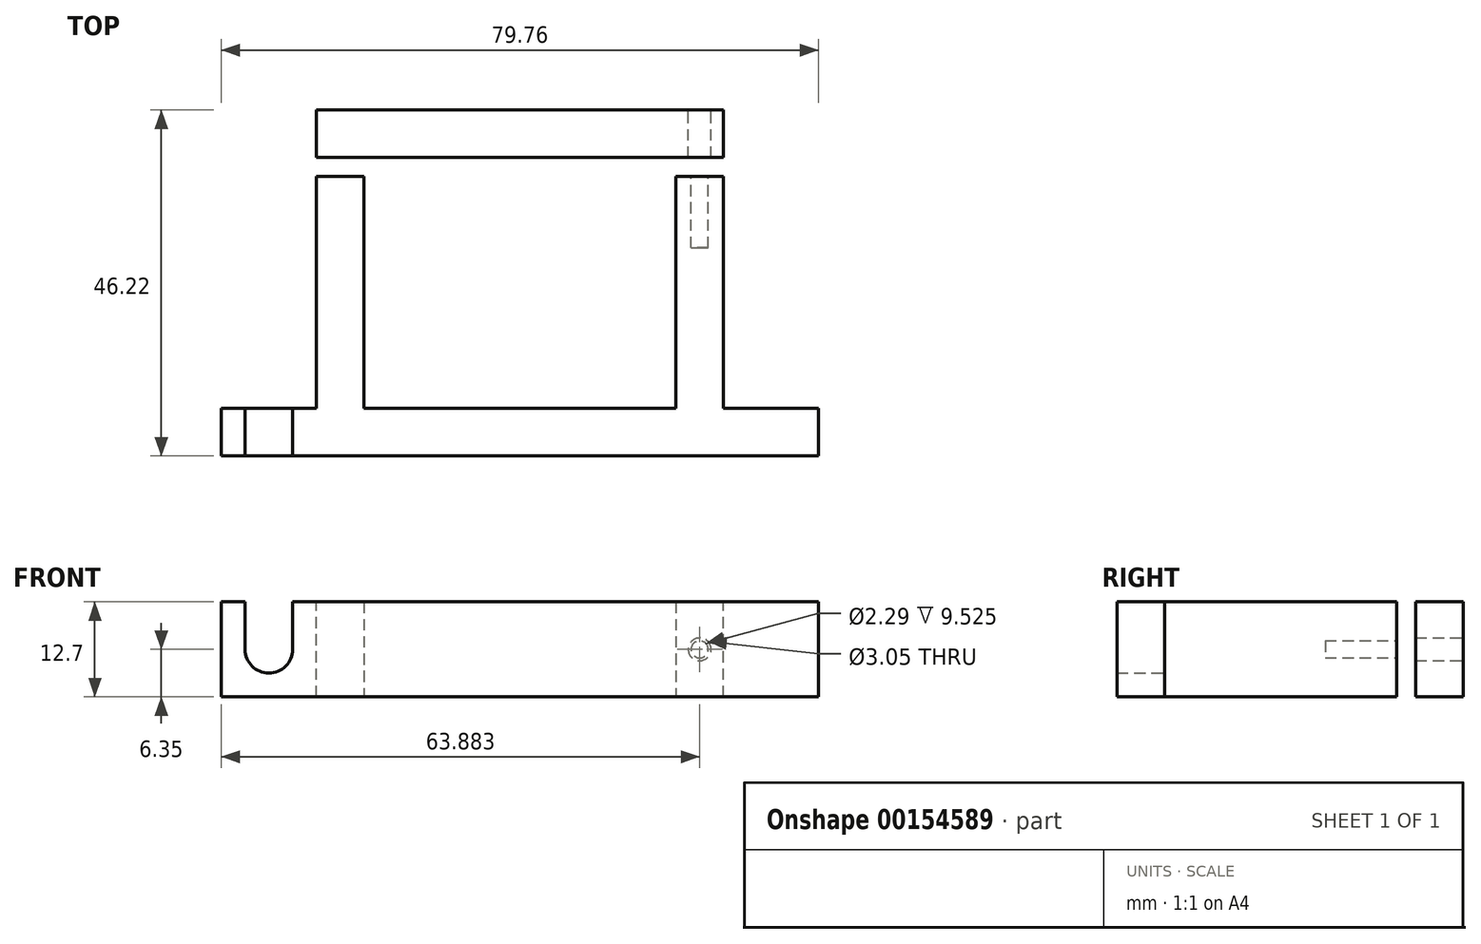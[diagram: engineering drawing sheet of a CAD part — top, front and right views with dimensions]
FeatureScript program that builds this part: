
annotation { "Feature Type Name" : "Feature", "Feature Type Description" : "" }
export const myFeature = defineFeature(function(context is Context, id is Id, definition is map)
    precondition{}
    {
        {
            var Q0;
            Q0=qCreatedBy(makeId("Top.planeOp"),FACE);
            var sketch = newSketch(context, id + "F0", { "sketchPlane" : qUnion([Q0])});
            skLineSegment(sketch, "E0.bottom", {"start": v(-20.83, 16.76) * mm, "end": v(20.83, 16.76) * mm});
            skLineSegment(sketch, "E0.top", {"start": v(-20.83, -16.76) * mm, "end": v(20.83, -16.76) * mm});
            skLineSegment(sketch, "E0.left", {"start": v(-20.83, 16.76) * mm, "end": v(-20.83, -16.76) * mm});
            skLineSegment(sketch, "E0.right", {"start": v(20.83, 16.76) * mm, "end": v(20.83, -16.76) * mm});
            skPoint(sketch, "E0.middle", {"position": v(0, 0) * mm});
            skLineSegment(sketch, "E1.0", {"start": v(27.18, 23.11) * mm, "end": v(27.18, -23.11) * mm});
            skLineSegment(sketch, "E1.1", {"start": v(-27.18, 23.11) * mm, "end": v(27.18, 23.11) * mm});
            skLineSegment(sketch, "E1.2", {"start": v(-27.18, 23.11) * mm, "end": v(-27.18, -23.11) * mm});
            skLineSegment(sketch, "E1.3", {"start": v(-27.18, -23.11) * mm, "end": v(27.18, -23.11) * mm});
            skLineSegment(sketch, "E2", {"start": v(-27.18, -16.76) * mm, "end": v(-39.88, -16.76) * mm});
            skLineSegment(sketch, "E3", {"start": v(-39.88, -16.76) * mm, "end": v(-39.88, -23.11) * mm});
            skLineSegment(sketch, "E4", {"start": v(-39.88, -23.11) * mm, "end": v(-27.18, -23.11) * mm});
            skLineSegment(sketch, "E5", {"start": v(27.18, -16.76) * mm, "end": v(39.88, -16.76) * mm});
            skLineSegment(sketch, "E6", {"start": v(39.88, -16.76) * mm, "end": v(39.88, -23.11) * mm});
            skLineSegment(sketch, "E7", {"start": v(39.88, -23.11) * mm, "end": v(27.18, -23.11) * mm});
            skSolve(sketch);
        }
        {
            var Q0;
            Q0 = qSketchRegion(id + "F0", true);
            extrude(context, id + "F1", {"entities" : qUnion([Q0]), "depth" : 12.7 * mm});
        }
        {
            var Q0;
            Q0=makeQuery(id+"F1.opExtrude","SWEPT_FACE",FACE,{"disambiguationData":[OSD([sQuery(id+"F0.wireOp",EDGE,"E2")])]});
            var sketch = newSketch(context, id + "F2", { "sketchPlane" : qUnion([Q0])});
            skLineSegment(sketch, "E8", {"start": v(39.88, 12.7) * mm, "end": v(27.18, 0) * mm, "construction": true});
            skArc(sketch, "E9", {"start": v(30.35, 6.35) * mm, "mid": v(33.53, 3.17) * mm, "end": v(36.7, 6.35) * mm});
            skPoint(sketch, "E9.startSnap0", {"position": v(33.53, 6.35) * mm});
            skLineSegment(sketch, "E10", {"start": v(36.7, 6.35) * mm, "end": v(36.7, 12.7) * mm});
            skLineSegment(sketch, "E11", {"start": v(36.7, 12.7) * mm, "end": v(30.35, 12.7) * mm});
            skLineSegment(sketch, "E12", {"start": v(30.35, 12.7) * mm, "end": v(30.35, 6.35) * mm});
            skSolve(sketch);
        }
        {
            var Q0;
            Q0 = qSketchRegion(id + "F2", true);
            extrude(context, id + "F3", {"entities" : qUnion([Q0]), "operationType" : NewBodyOperationType.REMOVE, "endBound" : BoundingType.THROUGH_ALL, "oppositeDirection" : true, "depth" : 25.4 * mm});
        }
        {
            var Q0;
            {var subQ0=sQuery(id+"F0.wireOp",EDGE,"E7");var subQ1=sQuery(id+"F0.wireOp",EDGE,"E4");var subQ2=sQuery(id+"F0.wireOp",EDGE,"E1.3");var subQ4=sQuery(id+"F0.wireOp",EDGE,"E1.2");var subQ6=sQuery(id+"F0.wireOp",EDGE,"E1.1");var subQ8=sQuery(id+"F0.wireOp",EDGE,"E1.0");var subQ10=sQuery(id+"F0.wireOp",EDGE,"E0.bottom");var subQ11=makeQuery(id+"F1.opExtrude","SWEPT_FACE",FACE,{"disambiguationData":[OSD([subQ10])]});var subQ12=sQuery(id+"F0.wireOp",EDGE,"E2");var subQ14=sQuery(id+"F0.wireOp",EDGE,"E0.top");var subQ16=sQuery(id+"F0.wireOp",EDGE,"E0.left");var subQ18=sQuery(id+"F0.wireOp",EDGE,"E5");var subQ22=sQuery(id+"F0.wireOp",EDGE,"E0.right");var subQ24=sQuery(id+"F0.wireOp",EDGE,"E6");Q0=makeQuery(id+"FPNAXTvCDZx5EIz_1.1.F3.boolean.opBoolean","SPLIT",FACE,{"disambiguationData":[TD([subQ11])],"derivedFrom":makeQuery(id+"F3.boolean.opBoolean","SPLIT",FACE,{"disambiguationData":[TD([subQ11])],"derivedFrom":makeQuery(id+"F1.opExtrude","CAP_FACE",FACE,{"disambiguationData":[OSD([subQ10,subQ14,subQ16,subQ22,subQ8,subQ6,subQ4,subQ2,subQ12,sQuery(id+"F0.wireOp",EDGE,"E3"),subQ1,subQ18,subQ24,subQ0])],"isStart":false})})});}
            var sketch = newSketch(context, id + "F4", { "sketchPlane" : qUnion([Q0])});
            skLineSegment(sketch, "E13.bottom", {"start": v(-27.18, 16.76) * mm, "end": v(27.18, 16.76) * mm});
            skLineSegment(sketch, "E13.top", {"start": v(-27.18, 14.22) * mm, "end": v(27.18, 14.22) * mm});
            skLineSegment(sketch, "E13.left", {"start": v(-27.18, 16.76) * mm, "end": v(-27.18, 14.22) * mm});
            skLineSegment(sketch, "E13.right", {"start": v(27.18, 16.76) * mm, "end": v(27.18, 14.22) * mm});
            skSolve(sketch);
        }
        {
            var Q0;
            Q0 = qSketchRegion(id + "F4", true);
            extrude(context, id + "F5", {"entities" : qUnion([Q0]), "operationType" : NewBodyOperationType.REMOVE, "endBound" : BoundingType.THROUGH_ALL, "oppositeDirection" : true, "depth" : 25.4 * mm});
        }
        {
            var Q0;
            {var subQ10=sQuery(id+"F0.wireOp",EDGE,"E0.right");Q0=makeQuery(id+"F5.boolean.opBoolean","COPY",FACE,{"disambiguationData":[TD([makeQuery(id+"F1.opExtrude","SWEPT_FACE",FACE,{"disambiguationData":[OSD([subQ10])]})])],"derivedFrom":makeQuery(id+"F5.opExtrude","SWEPT_FACE",FACE,{"disambiguationData":[OSD([sQuery(id+"F4.wireOp",EDGE,"E13.top")])]})});}
            var sketch = newSketch(context, id + "F6", { "sketchPlane" : qUnion([Q0])});
            skLineSegment(sketch, "E14", {"start": v(-24, 12.7) * mm, "end": v(-24, 0) * mm, "construction": true});
            skCircle(sketch, "E15", {"center": v(-24, 6.35) * mm, "radius": 1.14 * mm});
            skSolve(sketch);
        }
        {
            var Q0;
            Q0=makeQuery(id+"F6.imprint","IMPRINT",FACE,{"disambiguationData":[TD([[makeQuery(id+"F6.imprint","IMPRINT",EDGE,{"derivedFrom":sQuery(id+"F6.wireOp",EDGE,"E15")}),1.0]])]});
            var Q1;
            Q1=sQuery(id+"F6.wireOp",EDGE,"E15");
            extrude(context, id + "F7", {"entities" : qUnion([Q0]), "operationType" : NewBodyOperationType.REMOVE, "surfaceEntities" : qUnion([Q1]), "oppositeDirection" : true, "depth" : 9.52 * mm});
        }
        {
            var Q0;
            Q0=makeQuery(id+"F1.opExtrude","SWEPT_FACE",FACE,{"disambiguationData":[OSD([sQuery(id+"F0.wireOp",EDGE,"E1.1")])]});
            var sketch = newSketch(context, id + "F8", { "sketchPlane" : qUnion([Q0])});
            skCircle(sketch, "E16", {"center": v(-24, 6.35) * mm, "radius": 1.52 * mm});
            skSolve(sketch);
        }
        {
            var Q0;
            Q0=makeQuery(id+"F8.imprint","IMPRINT",FACE,{"disambiguationData":[TD([[makeQuery(id+"F8.imprint","IMPRINT",EDGE,{"derivedFrom":sQuery(id+"F8.wireOp",EDGE,"E16")}),1.0]])]});
            extrude(context, id + "F9", {"entities" : qUnion([Q0]), "operationType" : NewBodyOperationType.REMOVE, "endBound" : BoundingType.UP_TO_NEXT, "oppositeDirection" : true, "depth" : 25.4 * mm});
        }
    });
